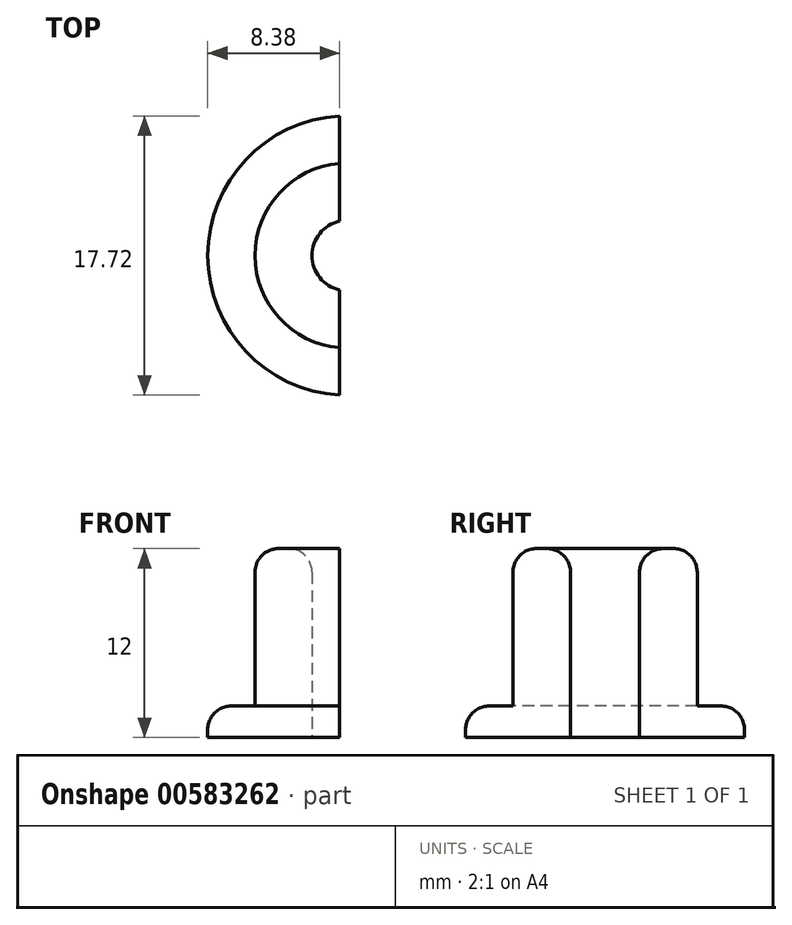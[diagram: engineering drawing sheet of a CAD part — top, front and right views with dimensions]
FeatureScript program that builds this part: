
annotation { "Feature Type Name" : "Feature", "Feature Type Description" : "" }
export const myFeature = defineFeature(function(context is Context, id is Id, definition is map)
    precondition{}
    {
        {
            var Q0;
            Q0=qCreatedBy(makeId("Top.planeOp"),FACE);
            var sketch = newSketch(context, id + "F0", { "sketchPlane" : qUnion([Q0])});
            skCircle(sketch, "E0", {"center": v(0, 0) * mm, "radius": 2.25 * mm});
            skCircle(sketch, "E1", {"center": v(0, 0) * mm, "radius": 5.88 * mm});
            skLineSegment(sketch, "E2", {"start": v(0, 0) * mm, "end": v(0, 9.95) * mm, "construction": true});
            skLineSegment(sketch, "E3", {"start": v(-0.5, 8.86) * mm, "end": v(-0.5, -8.86) * mm});
            skCircle(sketch, "E4", {"center": v(0, 0) * mm, "radius": 8.88 * mm});
            skSolve(sketch);
        }
        {
            var Q0;
            {var subQ0=sQuery(id+"F0.wireOp",EDGE,"E3");var subQ1=sQuery(id+"F0.wireOp",EDGE,"E0");var subQ2=makeQuery(id+"F0.imprint","INTERSECT",VERTEX,{"disambiguationData":[OD(0.0)],"derivedFrom":[subQ1,subQ0]});Q0=makeQuery(id+"F0.imprint","IMPRINT",FACE,{"disambiguationData":[TD([[makeQuery(id+"F0.imprint","IMPRINT",EDGE,{"disambiguationData":[TD([[subQ2,-1.0]])],"derivedFrom":subQ1}),-1.0]])]});}
            extrude(context, id + "F1", {"entities" : qUnion([Q0]), "depth" : 12 * mm, "offsetDistance" : 25 * mm});
        }
        {
            var Q0;
            {var subQ0=sQuery(id+"F0.wireOp",EDGE,"E3");var subQ1=sQuery(id+"F0.wireOp",EDGE,"E1");var subQ2=makeQuery(id+"F0.imprint","INTERSECT",VERTEX,{"disambiguationData":[OD(0.0)],"derivedFrom":[subQ1,subQ0]});Q0=makeQuery(id+"F0.imprint","IMPRINT",FACE,{"disambiguationData":[TD([[makeQuery(id+"F0.imprint","IMPRINT",EDGE,{"disambiguationData":[TD([[subQ2,-1.0]])],"derivedFrom":subQ1}),-1.0]])]});}
            extrude(context, id + "F2", {"entities" : qUnion([Q0]), "operationType" : NewBodyOperationType.ADD, "depth" : 2 * mm, "offsetDistance" : 25 * mm});
        }
        {
            var Q0;
            Q0=makeQuery(id+"F2.opExtrude","CAP_EDGE",EDGE,{"disambiguationData":[OSD([sQuery(id+"F0.wireOp",EDGE,"E1")])],"isStart":false});
            var Q1;
            Q1=makeQuery(id+"F2.opExtrude","CAP_EDGE",EDGE,{"disambiguationData":[OSD([sQuery(id+"F0.wireOp",EDGE,"E4")])],"isStart":false});
            var Q2;
            Q2=makeQuery(id+"F1.opExtrude","CAP_EDGE",EDGE,{"disambiguationData":[OSD([sQuery(id+"F0.wireOp",EDGE,"E1")])],"isStart":false});
            var Q3;
            Q3=makeQuery(id+"F1.opExtrude","CAP_EDGE",EDGE,{"disambiguationData":[OSD([sQuery(id+"F0.wireOp",EDGE,"E0")])],"isStart":false});
            fillet(context, id + "F3", {"entities" : qUnion([Q0, Q1, Q2, Q3]), "radius" : 1.5 * mm, "tangentPropagation" : true, "allowEdgeOverflow" : false});
        }
    });
